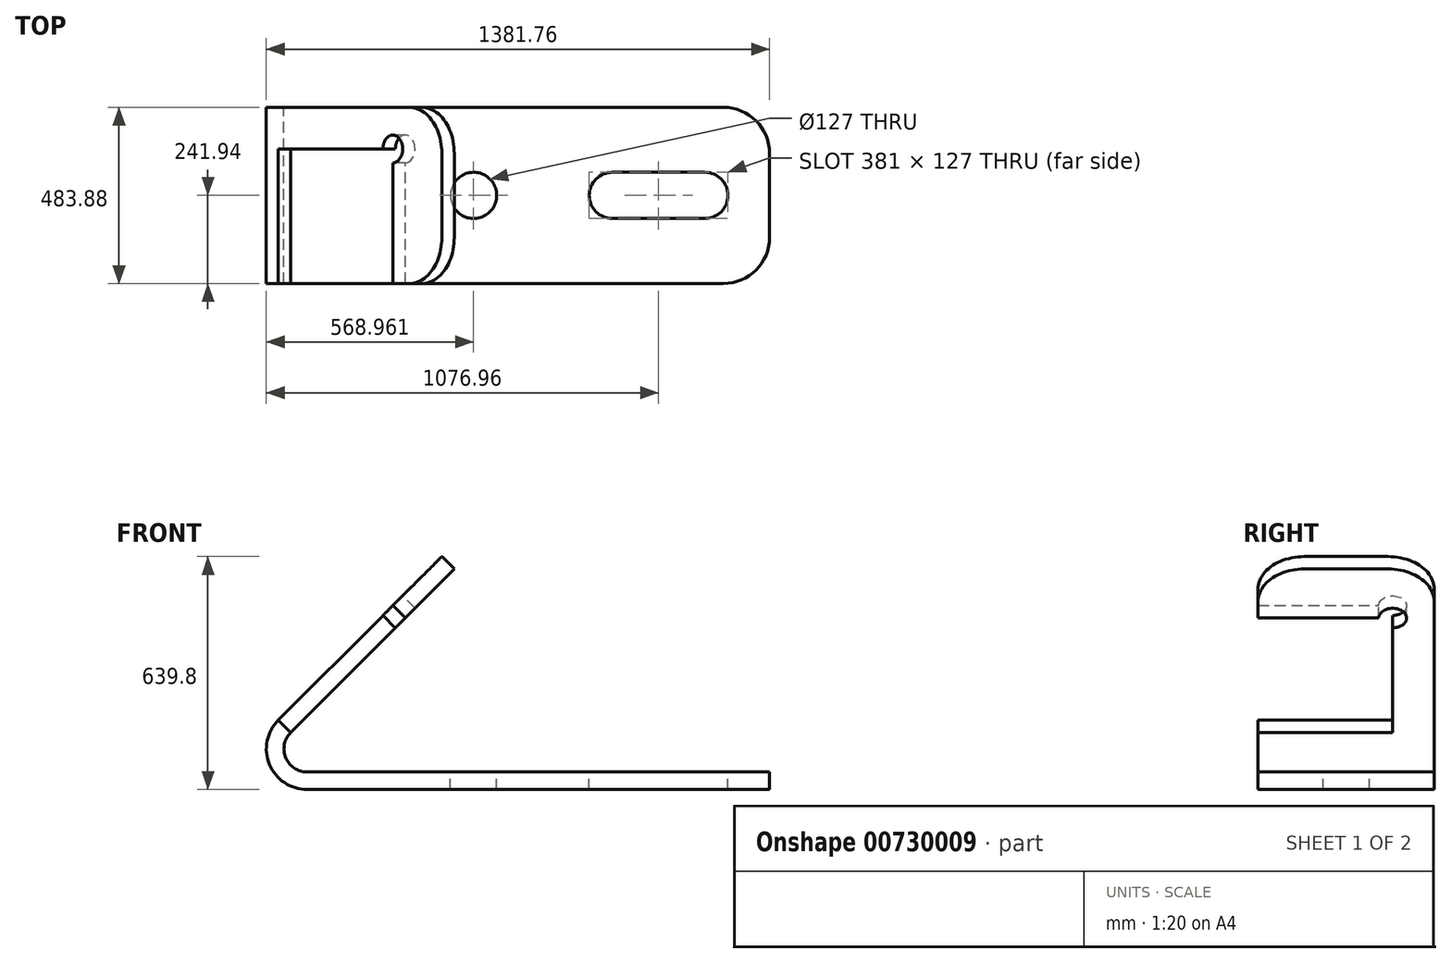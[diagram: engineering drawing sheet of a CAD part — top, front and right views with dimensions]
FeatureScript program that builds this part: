
annotation { "Feature Type Name" : "Feature", "Feature Type Description" : "" }
export const myFeature = defineFeature(function(context is Context, id is Id, definition is map)
    precondition{}
    {
        {
            var Q0;
            Q0=qCreatedBy(makeId("Front.planeOp"),FACE);
            var sketch = newSketch(context, id + "F0", { "sketchPlane" : qUnion([Q0])});
            skArc(sketch, "E0", {"start": v(-590.08, 79.03) * mm, "mid": v(-614.3, -42.77) * mm, "end": v(-511.05, -111.76) * mm});
            skLineSegment(sketch, "E1", {"start": v(-590.08, 79.03) * mm, "end": v(-141.06, 528.04) * mm});
            skLineSegment(sketch, "E2", {"start": v(-511.05, -111.76) * mm, "end": v(758.95, -111.76) * mm});
            skArc(sketch, "E3", {"start": v(-555.95, 44.9) * mm, "mid": v(-569.72, -24.3) * mm, "end": v(-511.05, -63.5) * mm});
            skLineSegment(sketch, "E4", {"start": v(-511.05, -63.5) * mm, "end": v(758.95, -63.5) * mm});
            skLineSegment(sketch, "E5", {"start": v(-555.95, 44.9) * mm, "end": v(-106.94, 493.91) * mm});
            skLineSegment(sketch, "E6", {"start": v(-141.06, 528.04) * mm, "end": v(-106.94, 493.91) * mm});
            skLineSegment(sketch, "E7", {"start": v(758.95, -63.5) * mm, "end": v(758.95, -111.76) * mm});
            skLineSegment(sketch, "E8", {"start": v(-511.05, -63.5) * mm, "end": v(758.95, -63.5) * mm, "construction": true});
            skSolve(sketch);
        }
        {
            var Q0;
            Q0=makeQuery(id+"F0.imprint","IMPRINT",FACE,{"disambiguationData":[TD([[makeQuery(id+"F0.imprint","IMPRINT",EDGE,{"derivedFrom":sQuery(id+"F0.wireOp",EDGE,"E0")}),1.0]])]});
            extrude(context, id + "F1", {"entities" : qUnion([Q0]), "endBound" : BoundingType.SYMMETRIC, "depth" : 483.87 * mm, "offsetDistance" : 25.4 * mm});
        }
        {
            var Q0;
            Q0=makeQuery(id+"F1.opExtrude","SWEPT_FACE",FACE,{"disambiguationData":[OSD([sQuery(id+"F0.wireOp",EDGE,"E4")])]});
            var sketch = newSketch(context, id + "F2", { "sketchPlane" : qUnion([Q0])});
            skLineSegment(sketch, "E9", {"start": v(758.95, 0) * mm, "end": v(-80, 0) * mm, "construction": true});
            skArc(sketch, "E10", {"start": v(581.15, -63.5) * mm, "mid": v(644.65, 0) * mm, "end": v(581.15, 63.5) * mm});
            skArc(sketch, "E11", {"start": v(327.15, 63.5) * mm, "mid": v(263.65, 0) * mm, "end": v(327.15, -63.5) * mm});
            skLineSegment(sketch, "E12", {"start": v(327.15, 63.5) * mm, "end": v(581.15, 63.5) * mm});
            skLineSegment(sketch, "E13", {"start": v(581.15, -63.5) * mm, "end": v(327.15, -63.5) * mm});
            skCircle(sketch, "E14", {"center": v(-53.85, 0) * mm, "radius": 63.5 * mm});
            skSolve(sketch);
        }
        {
            var Q0;
            Q0=makeQuery(id+"F1.opExtrude","CAP_EDGE",EDGE,{"disambiguationData":[OSD([sQuery(id+"F0.wireOp",EDGE,"E7")])],"isStart":true});
            var Q1;
            Q1=makeQuery(id+"F1.opExtrude","CAP_EDGE",EDGE,{"disambiguationData":[OSD([sQuery(id+"F0.wireOp",EDGE,"E7")])],"isStart":false});
            fillet(context, id + "F3", {"entities" : qUnion([Q0, Q1]), "radius" : 127 * mm, "tangentPropagation" : true, "allowEdgeOverflow" : false});
        }
        {
            var Q0;
            Q0=makeQuery(id+"F2.imprint","IMPRINT",FACE,{"disambiguationData":[TD([[makeQuery(id+"F2.imprint","IMPRINT",EDGE,{"derivedFrom":sQuery(id+"F2.wireOp",EDGE,"E10")}),1.0]])]});
            var Q1;
            Q1=makeQuery(id+"F2.imprint","IMPRINT",FACE,{"disambiguationData":[TD([[makeQuery(id+"F2.imprint","IMPRINT",EDGE,{"derivedFrom":sQuery(id+"F2.wireOp",EDGE,"E14")}),1.0]])]});
            extrude(context, id + "F4", {"entities" : qUnion([Q0, Q1]), "operationType" : NewBodyOperationType.REMOVE, "oppositeDirection" : true, "depth" : 1264.92 * mm, "offsetDistance" : 25.4 * mm});
        }
        {
            var Q0;
            Q0=makeQuery(id+"F1.opExtrude","SWEPT_FACE",FACE,{"disambiguationData":[OSD([sQuery(id+"F0.wireOp",EDGE,"E1")])]});
            var sketch = newSketch(context, id + "F5", { "sketchPlane" : qUnion([Q0])});
            skLineSegment(sketch, "E15", {"start": v(127.64, 273.63) * mm, "end": v(127.64, -361.37) * mm});
            skLineSegment(sketch, "E16", {"start": v(241.94, 83.13) * mm, "end": v(-241.94, 83.13) * mm});
            skLineSegment(sketch, "E17", {"start": v(-127.64, 273.63) * mm, "end": v(-127.64, -361.37) * mm});
            skCircle(sketch, "E18", {"center": v(-127.64, 83.13) * mm, "radius": 38.1 * mm});
            skCircle(sketch, "E19", {"center": v(127.64, 83.13) * mm, "radius": 38.1 * mm});
            skSolve(sketch);
        }
        {
            var Q0;
            {var subQ0=sQuery(id+"F5.wireOp",EDGE,"E18");var subQ1=sQuery(id+"F5.wireOp",EDGE,"E16");var subQ2=makeQuery(id+"F5.imprint","INTERSECT",VERTEX,{"disambiguationData":[OD(0.0)],"derivedFrom":[subQ1,subQ0]});Q0=makeQuery(id+"F5.imprint","IMPRINT",FACE,{"disambiguationData":[TD([[makeQuery(id+"F5.imprint","IMPRINT",EDGE,{"disambiguationData":[TD([[subQ2,-1.0]])],"derivedFrom":subQ1}),-1.0]])]});}
            var Q1;
            {var subQ0=sQuery(id+"F5.wireOp",EDGE,"E18");var subQ1=sQuery(id+"F5.wireOp",EDGE,"E16");var subQ2=makeQuery(id+"F5.imprint","INTERSECT",VERTEX,{"disambiguationData":[OD(0.0)],"derivedFrom":[subQ1,subQ0]});Q1=makeQuery(id+"F5.imprint","IMPRINT",FACE,{"disambiguationData":[TD([[makeQuery(id+"F5.imprint","IMPRINT",EDGE,{"disambiguationData":[TD([[subQ2,-1.0]])],"derivedFrom":subQ1}),1.0]])]});}
            var Q2;
            {var subQ0=sQuery(id+"F5.wireOp",EDGE,"E17");var subQ1=sQuery(id+"F5.wireOp",EDGE,"E16");var subQ2=makeQuery(id+"F5.imprint","INTERSECT",VERTEX,{"derivedFrom":[subQ1,subQ0]});Q2=makeQuery(id+"F5.imprint","IMPRINT",FACE,{"disambiguationData":[TD([[makeQuery(id+"F5.imprint","IMPRINT",EDGE,{"disambiguationData":[TD([[subQ2,-1.0]])],"derivedFrom":subQ1}),1.0]])]});}
            var Q3;
            {var subQ0=sQuery(id+"F5.wireOp",EDGE,"E17");var subQ1=sQuery(id+"F5.wireOp",EDGE,"E16");var subQ2=makeQuery(id+"F5.imprint","INTERSECT",VERTEX,{"derivedFrom":[subQ1,subQ0]});Q3=makeQuery(id+"F5.imprint","IMPRINT",FACE,{"disambiguationData":[TD([[makeQuery(id+"F5.imprint","IMPRINT",EDGE,{"disambiguationData":[TD([[subQ2,-1.0]])],"derivedFrom":subQ1}),-1.0]])]});}
            var Q4;
            {var subQ0=sQuery(id+"F5.wireOp",EDGE,"E16");var subQ1=sQuery(id+"F5.wireOp",EDGE,"E15");var subQ2=makeQuery(id+"F5.imprint","INTERSECT",VERTEX,{"derivedFrom":[subQ1,subQ0]});Q4=makeQuery(id+"F5.imprint","IMPRINT",FACE,{"disambiguationData":[TD([[makeQuery(id+"F5.imprint","IMPRINT",EDGE,{"disambiguationData":[TD([[subQ2,-1.0]])],"derivedFrom":subQ1}),-1.0]])]});}
            var Q5;
            {var subQ0=sQuery(id+"F5.wireOp",EDGE,"E19");var subQ1=sQuery(id+"F5.wireOp",EDGE,"E15");var subQ2=makeQuery(id+"F5.imprint","INTERSECT",VERTEX,{"disambiguationData":[OD(0.0)],"derivedFrom":[subQ1,subQ0]});Q5=makeQuery(id+"F5.imprint","IMPRINT",FACE,{"disambiguationData":[TD([[makeQuery(id+"F5.imprint","IMPRINT",EDGE,{"disambiguationData":[TD([[subQ2,-1.0]])],"derivedFrom":subQ1}),-1.0]])]});}
            var Q6;
            {var subQ0=sQuery(id+"F5.wireOp",EDGE,"E16");var subQ1=sQuery(id+"F5.wireOp",EDGE,"E15");var subQ2=makeQuery(id+"F5.imprint","INTERSECT",VERTEX,{"derivedFrom":[subQ1,subQ0]});Q6=makeQuery(id+"F5.imprint","IMPRINT",FACE,{"disambiguationData":[TD([[makeQuery(id+"F5.imprint","IMPRINT",EDGE,{"disambiguationData":[TD([[subQ2,-1.0]])],"derivedFrom":subQ1}),1.0]])]});}
            var Q7;
            {var subQ0=sQuery(id+"F5.wireOp",EDGE,"E19");var subQ1=sQuery(id+"F5.wireOp",EDGE,"E15");var subQ2=makeQuery(id+"F5.imprint","INTERSECT",VERTEX,{"disambiguationData":[OD(0.0)],"derivedFrom":[subQ1,subQ0]});Q7=makeQuery(id+"F5.imprint","IMPRINT",FACE,{"disambiguationData":[TD([[makeQuery(id+"F5.imprint","IMPRINT",EDGE,{"disambiguationData":[TD([[subQ2,-1.0]])],"derivedFrom":subQ1}),1.0]])]});}
            extrude(context, id + "F6", {"entities" : qUnion([Q0, Q1, Q2, Q3, Q4, Q5, Q6, Q7]), "operationType" : NewBodyOperationType.REMOVE, "oppositeDirection" : true, "depth" : 76.2 * mm, "offsetDistance" : 25.4 * mm});
        }
        {
            var Q0;
            Q0=makeQuery(id+"F1.opExtrude","CAP_EDGE",EDGE,{"disambiguationData":[OSD([sQuery(id+"F0.wireOp",EDGE,"E6")])],"isStart":false});
            var Q1;
            Q1=makeQuery(id+"F1.opExtrude","CAP_EDGE",EDGE,{"disambiguationData":[OSD([sQuery(id+"F0.wireOp",EDGE,"E6")])],"isStart":true});
            fillet(context, id + "F7", {"entities" : qUnion([Q0, Q1]), "radius" : 127 * mm, "tangentPropagation" : true, "allowEdgeOverflow" : false});
        }
    });
